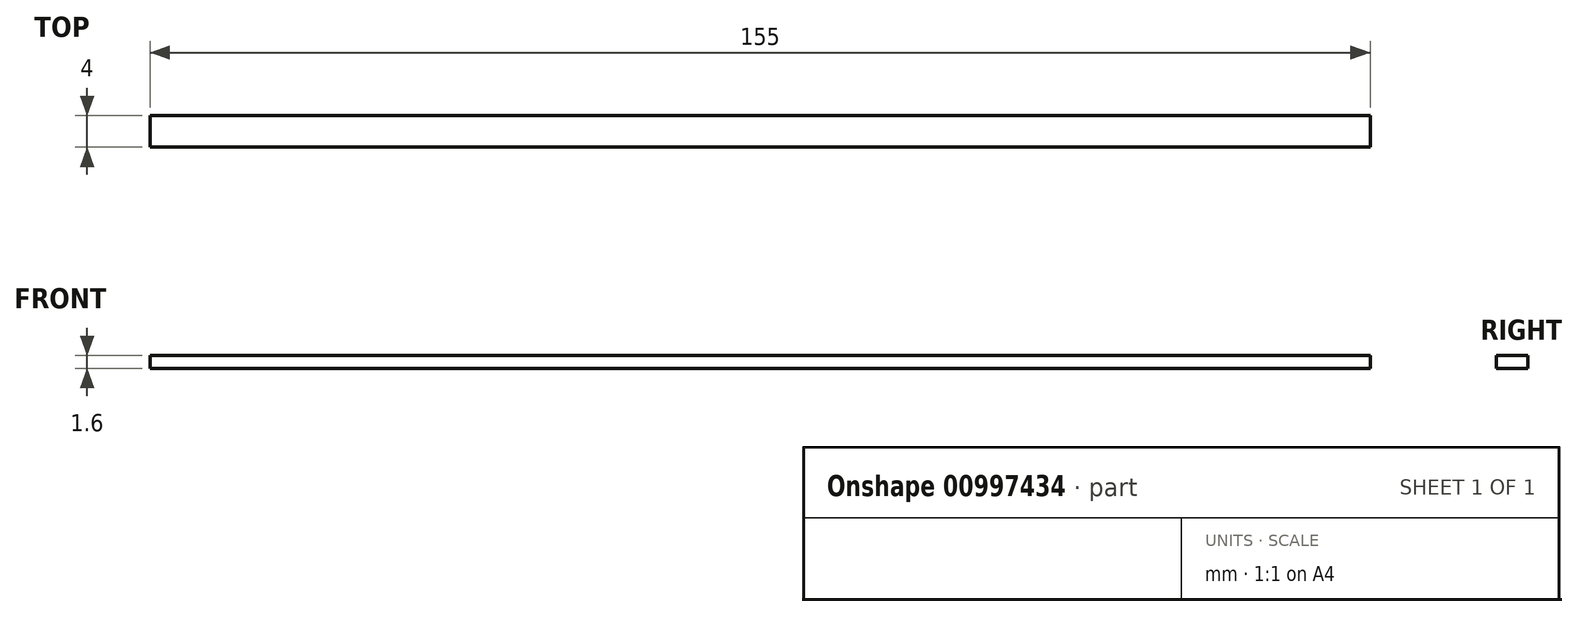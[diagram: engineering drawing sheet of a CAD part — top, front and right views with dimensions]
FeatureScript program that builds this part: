
annotation { "Feature Type Name" : "Feature", "Feature Type Description" : "" }
export const myFeature = defineFeature(function(context is Context, id is Id, definition is map)
    precondition{}
    {
        {
            var Q0;
            Q0=qCreatedBy(makeId("Top.planeOp"),FACE);
            var sketch = newSketch(context, id + "F0", { "sketchPlane" : qUnion([Q0])});
            skLineSegment(sketch, "E0.bottom", {"start": v(-89.85, -4.1) * mm, "end": v(65.15, -4.1) * mm});
            skLineSegment(sketch, "E0.top", {"start": v(-89.85, -8.1) * mm, "end": v(65.15, -8.1) * mm});
            skLineSegment(sketch, "E0.left", {"start": v(-89.85, -4.1) * mm, "end": v(-89.85, -8.1) * mm});
            skLineSegment(sketch, "E0.right", {"start": v(65.15, -4.1) * mm, "end": v(65.15, -8.1) * mm});
            skSolve(sketch);
        }
        {
            var Q0;
            Q0=makeQuery(id+"F0.imprint","IMPRINT",FACE,{"disambiguationData":[TD([[makeQuery(id+"F0.imprint","IMPRINT",EDGE,{"derivedFrom":sQuery(id+"F0.wireOp",EDGE,"E0.bottom")}),-1.0]])]});
            extrude(context, id + "F1", {"entities" : qUnion([Q0]), "depth" : 1.6 * mm, "offsetDistance" : 25 * mm});
        }
    });
